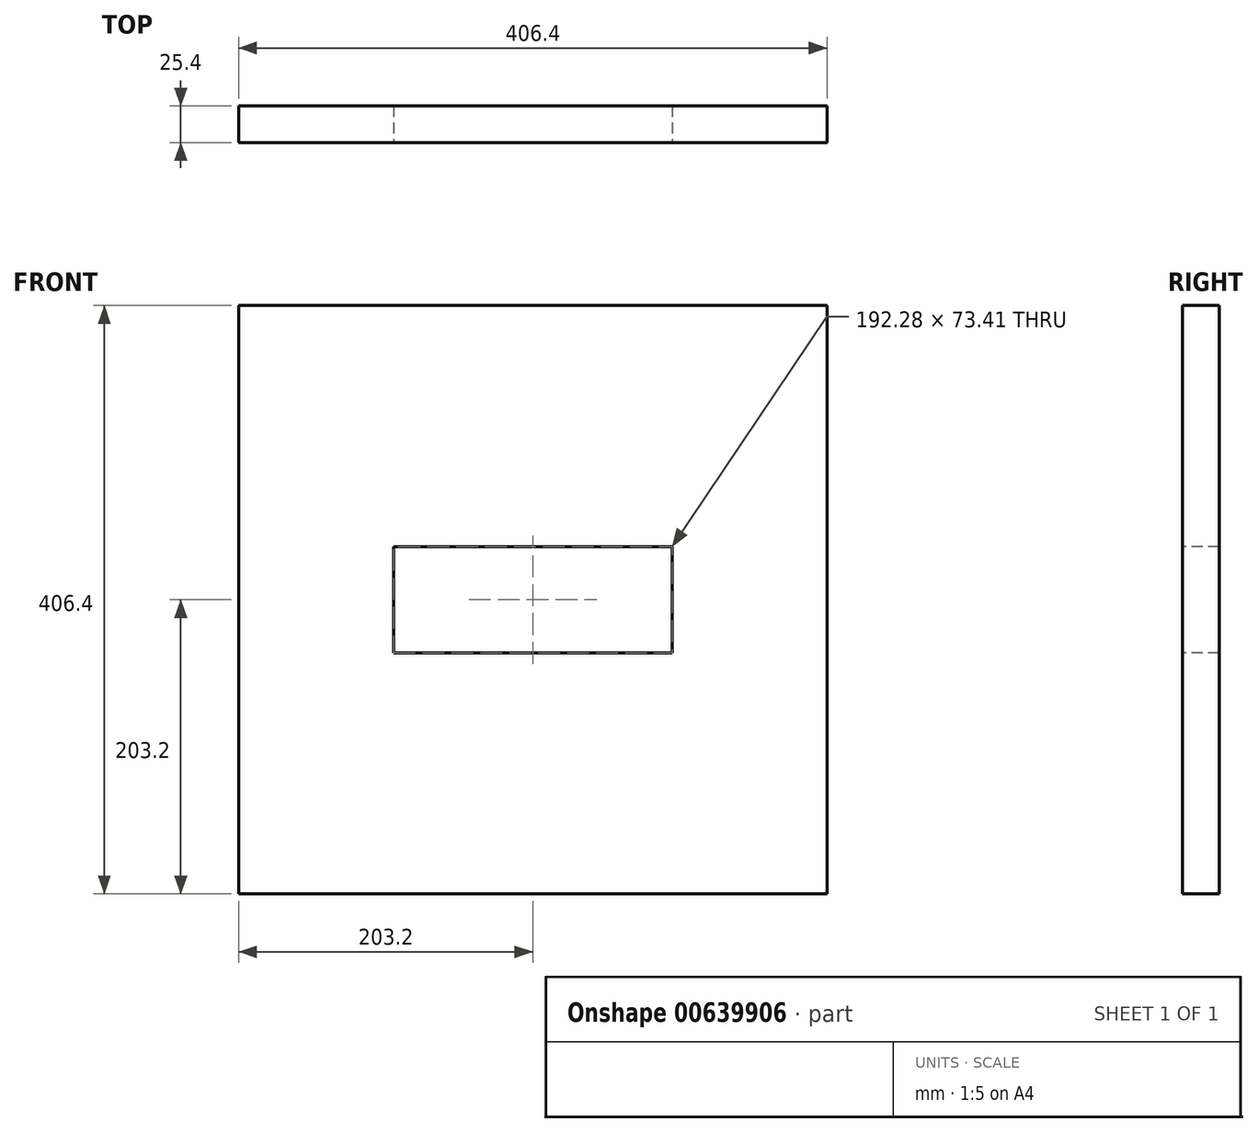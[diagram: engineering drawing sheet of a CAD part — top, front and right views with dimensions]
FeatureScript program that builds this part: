
annotation { "Feature Type Name" : "Feature", "Feature Type Description" : "" }
export const myFeature = defineFeature(function(context is Context, id is Id, definition is map)
    precondition{}
    {
        {
            var Q0;
            Q0=qCreatedBy(makeId("Front.planeOp"),FACE);
            var sketch = newSketch(context, id + "F0", { "sketchPlane" : qUnion([Q0])});
            skLineSegment(sketch, "E0.bottom", {"start": v(-203.2, 203.2) * mm, "end": v(203.2, 203.2) * mm});
            skLineSegment(sketch, "E0.top", {"start": v(-203.2, -203.2) * mm, "end": v(203.2, -203.2) * mm});
            skLineSegment(sketch, "E0.left", {"start": v(-203.2, 203.2) * mm, "end": v(-203.2, -203.2) * mm});
            skLineSegment(sketch, "E0.right", {"start": v(203.2, 203.2) * mm, "end": v(203.2, -203.2) * mm});
            skPoint(sketch, "E0.middle", {"position": v(0, 0) * mm});
            skSolve(sketch);
        }
        {
            var Q0;
            Q0=makeQuery(id+"F0.imprint","IMPRINT",FACE,{"disambiguationData":[TD([[makeQuery(id+"F0.imprint","IMPRINT",EDGE,{"derivedFrom":sQuery(id+"F0.wireOp",EDGE,"E0.bottom")}),-1.0]])]});
            extrude(context, id + "F1", {"entities" : qUnion([Q0]), "depth" : 25.4 * mm, "offsetDistance" : 25.4 * mm});
        }
        {
            var Q0;
            Q0=makeQuery(id+"F1.opExtrude","CAP_FACE",FACE,{"disambiguationData":[OSD([sQuery(id+"F0.wireOp",EDGE,"E0.bottom"),sQuery(id+"F0.wireOp",EDGE,"E0.top"),sQuery(id+"F0.wireOp",EDGE,"E0.left"),sQuery(id+"F0.wireOp",EDGE,"E0.right")])],"isStart":false});
            var sketch = newSketch(context, id + "F2", { "sketchPlane" : qUnion([Q0])});
            skLineSegment(sketch, "E1.bottom", {"start": v(96.14, -36.7) * mm, "end": v(-96.14, -36.7) * mm});
            skLineSegment(sketch, "E1.top", {"start": v(96.14, 36.7) * mm, "end": v(-96.14, 36.7) * mm});
            skLineSegment(sketch, "E1.left", {"start": v(96.14, -36.7) * mm, "end": v(96.14, 36.7) * mm});
            skLineSegment(sketch, "E1.right", {"start": v(-96.14, -36.7) * mm, "end": v(-96.14, 36.7) * mm});
            skPoint(sketch, "E1.middle", {"position": v(0, 0) * mm});
            skSolve(sketch);
        }
        {
            var Q0;
            Q0=makeQuery(id+"F2.imprint","IMPRINT",FACE,{"disambiguationData":[TD([[makeQuery(id+"F2.imprint","IMPRINT",EDGE,{"derivedFrom":sQuery(id+"F2.wireOp",EDGE,"E1.bottom")}),-1.0]])]});
            extrude(context, id + "F3", {"entities" : qUnion([Q0]), "operationType" : NewBodyOperationType.REMOVE, "endBound" : BoundingType.UP_TO_NEXT, "oppositeDirection" : true, "depth" : 25.4 * mm, "offsetDistance" : 25.4 * mm});
        }
    });
